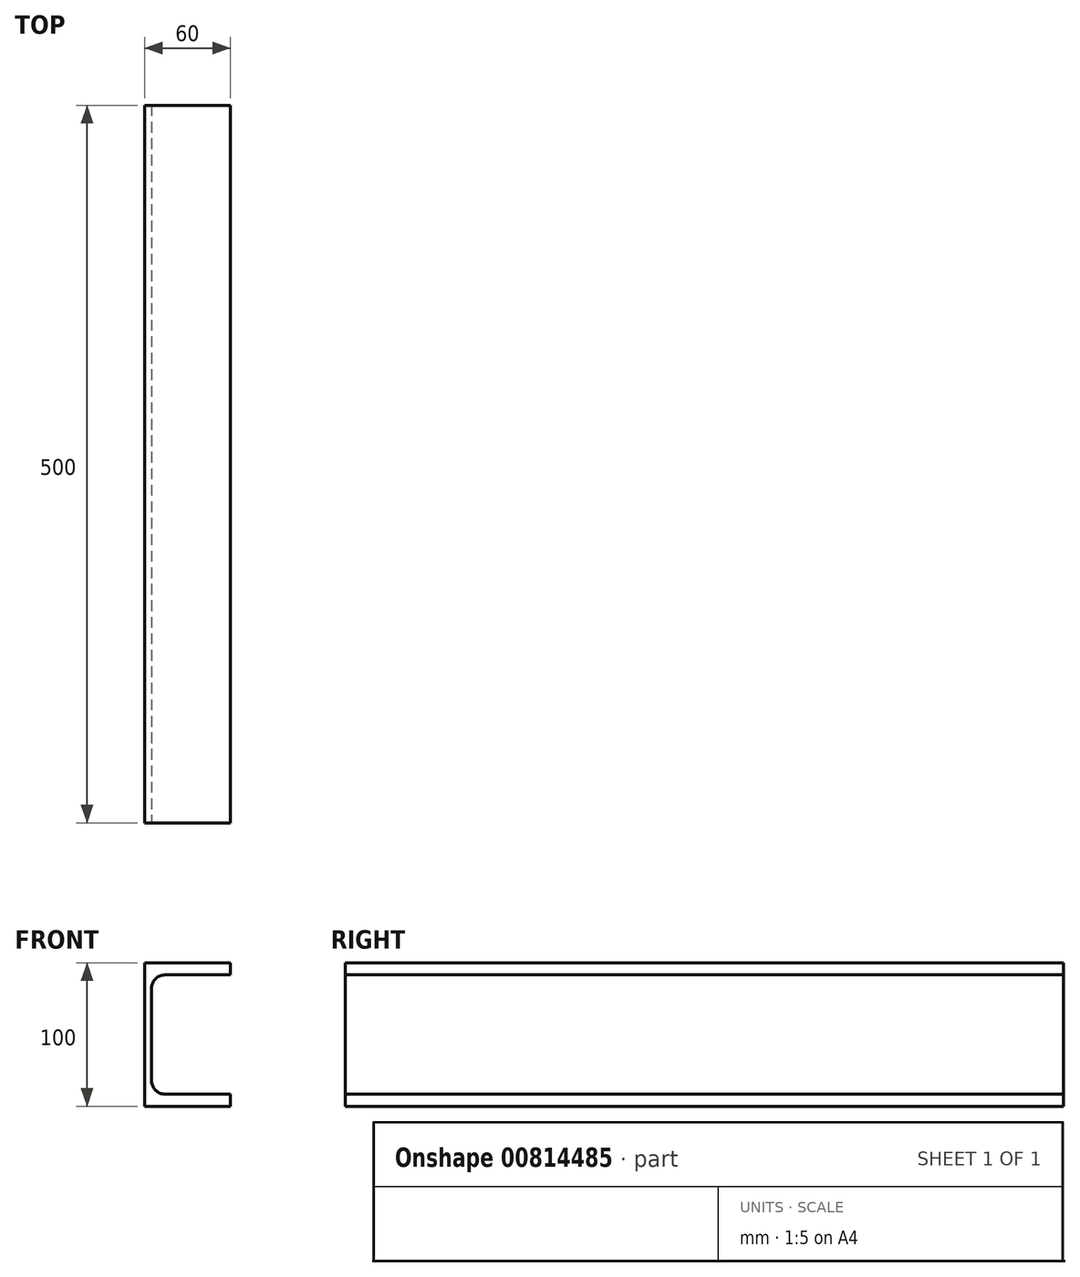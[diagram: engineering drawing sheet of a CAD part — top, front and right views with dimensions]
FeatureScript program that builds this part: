
annotation { "Feature Type Name" : "Feature", "Feature Type Description" : "" }
export const myFeature = defineFeature(function(context is Context, id is Id, definition is map)
    precondition{}
    {
        {
            var Q0;
            Q0=qCreatedBy(makeId("Front.planeOp"),FACE);
            var sketch = newSketch(context, id + "F0", { "sketchPlane" : qUnion([Q0])});
            skLineSegment(sketch, "E0", {"start": v(0, 0) * mm, "end": v(0, 50) * mm});
            skLineSegment(sketch, "E1", {"start": v(0, 50) * mm, "end": v(60, 50) * mm});
            skLineSegment(sketch, "E2", {"start": v(60, 50) * mm, "end": v(60, 41.5) * mm});
            skLineSegment(sketch, "E3", {"start": v(60, 41.5) * mm, "end": v(14, 41.5) * mm});
            skLineSegment(sketch, "E4", {"start": v(5, 32.5) * mm, "end": v(5, 0) * mm});
            skLineSegment(sketch, "E5", {"start": v(5, 0) * mm, "end": v(0, 0) * mm, "construction": true});
            skLineSegment(sketch, "E6.MirrorCS", {"start": v(60, -41.5) * mm, "end": v(14, -41.5) * mm});
            skLineSegment(sketch, "E7.MirrorCS", {"start": v(5, -32.5) * mm, "end": v(5, 0) * mm});
            skLineSegment(sketch, "E8.MirrorCS", {"start": v(0, 0) * mm, "end": v(0, -50) * mm});
            skLineSegment(sketch, "E9.MirrorCS", {"start": v(60, -50) * mm, "end": v(60, -41.5) * mm});
            skLineSegment(sketch, "E10.MirrorCS", {"start": v(0, -50) * mm, "end": v(60, -50) * mm});
            skPoint(sketch, "E11.visualSharp", {"position": v(5, 41.5) * mm});
            skArc(sketch, "E11.filletArc", {"start": v(14, 41.5) * mm, "mid": v(7.64, 38.86) * mm, "end": v(5, 32.5) * mm});
            skPoint(sketch, "E12.visualSharp", {"position": v(5, -41.5) * mm});
            skArc(sketch, "E12.filletArc", {"start": v(5, -32.5) * mm, "mid": v(7.64, -38.86) * mm, "end": v(14, -41.5) * mm});
            skSolve(sketch);
        }
        {
            assignVariable(context, id + "F1", {"name" : "Length", "anyValue" : 500});
        }
        {
            var Q0;
            Q0=makeQuery(id+"F0.imprint","IMPRINT",FACE,{"disambiguationData":[TD([[makeQuery(id+"F0.imprint","IMPRINT",EDGE,{"derivedFrom":sQuery(id+"F0.wireOp",EDGE,"E0")}),-1.0]])]});
            extrude(context, id + "F2", {"entities" : qUnion([Q0]), "oppositeDirection" : true, "depth" : (getVariable(context, 'Length')) * mm, "offsetDistance" : 25 * mm});
        }
    });
